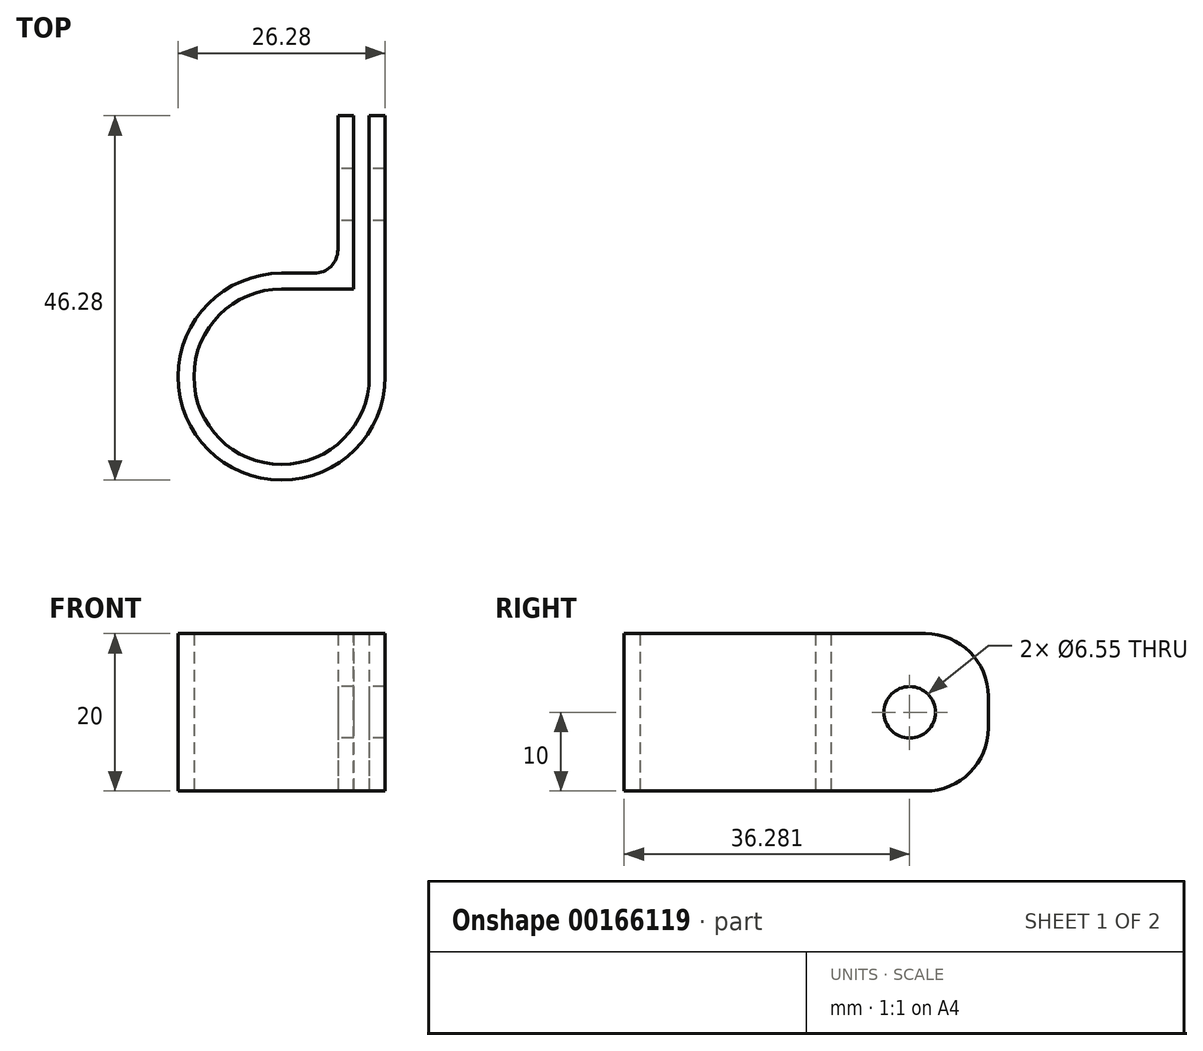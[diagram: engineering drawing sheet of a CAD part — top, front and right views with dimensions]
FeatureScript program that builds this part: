
annotation { "Feature Type Name" : "Feature", "Feature Type Description" : "" }
export const myFeature = defineFeature(function(context is Context, id is Id, definition is map)
    precondition{}
    {
        {
            var Q0;
            Q0=qCreatedBy(makeId("Top.planeOp"),FACE);
            var sketch = newSketch(context, id + "F0", { "sketchPlane" : qUnion([Q0])});
            skCircle(sketch, "E0", {"center": v(0, 0) * mm, "radius": 11.14 * mm});
            skCircle(sketch, "E1.0", {"center": v(0, 0) * mm, "radius": 13.14 * mm});
            skLineSegment(sketch, "E2", {"start": v(13.14, 0) * mm, "end": v(13.14, 33.14) * mm});
            skLineSegment(sketch, "E3", {"start": v(11.14, 0) * mm, "end": v(11.14, 33.14) * mm});
            skLineSegment(sketch, "E4", {"start": v(11.14, 33.14) * mm, "end": v(13.14, 33.14) * mm});
            skLineSegment(sketch, "E5", {"start": v(0, 13.14) * mm, "end": v(7.14, 13.14) * mm});
            skLineSegment(sketch, "E6", {"start": v(7.14, 13.14) * mm, "end": v(7.14, 33.14) * mm});
            skLineSegment(sketch, "E7", {"start": v(7.14, 33.14) * mm, "end": v(9.14, 33.14) * mm});
            skLineSegment(sketch, "E8", {"start": v(9.14, 33.14) * mm, "end": v(9.14, 9.44) * mm});
            skLineSegment(sketch, "E9", {"start": v(9.14, 33.14) * mm, "end": v(11.14, 33.14) * mm, "construction": true});
            skLineSegment(sketch, "E10", {"start": v(9.14, 9.44) * mm, "end": v(9.14, 6.37) * mm});
            skLineSegment(sketch, "E11", {"start": v(7.14, 23.14) * mm, "end": v(13.14, 23.14) * mm, "construction": true});
            skLineSegment(sketch, "E12", {"start": v(0, 11.14) * mm, "end": v(9.14, 11.14) * mm});
            skSolve(sketch);
        }
        {
            var Q0;
            {var subQ4=sQuery(id+"F0.wireOp",EDGE,"E0");var subQ7=sQuery(id+"F0.wireOp",EDGE,"E3");var subQ9=makeQuery(id+"F0.imprint","INTERSECT",VERTEX,{"derivedFrom":[subQ4,subQ7]});Q0=makeQuery(id+"F0.imprint","IMPRINT",FACE,{"disambiguationData":[TD([[makeQuery(id+"F0.imprint","IMPRINT",EDGE,{"disambiguationData":[TD([[subQ9,1.0]])],"derivedFrom":subQ4}),-1.0]])]});}
            var Q1;
            {var subQ1=sQuery(id+"F0.wireOp",EDGE,"E5");Q1=makeQuery(id+"F0.imprint","IMPRINT",FACE,{"disambiguationData":[TD([[makeQuery(id+"F0.imprint","IMPRINT",EDGE,{"derivedFrom":subQ1}),-1.0]])]});}
            var Q2;
            {var subQ0=sQuery(id+"F0.wireOp",EDGE,"E2");Q2=makeQuery(id+"F0.imprint","IMPRINT",FACE,{"disambiguationData":[TD([[makeQuery(id+"F0.imprint","IMPRINT",EDGE,{"derivedFrom":subQ0}),1.0]])]});}
            extrude(context, id + "F1", {"entities" : qUnion([Q0, Q1, Q2]), "endBound" : BoundingType.SYMMETRIC, "depth" : 20 * mm});
        }
        {
            var Q0;
            Q0=qCreatedBy(makeId("Right.planeOp"),FACE);
            var sketch = newSketch(context, id + "F2", { "sketchPlane" : qUnion([Q0])});
            skPoint(sketch, "E13.0", {"position": v(23.14, 0) * mm});
            skCircle(sketch, "E14", {"center": v(23.14, 0) * mm, "radius": 3.28 * mm});
            skSolve(sketch);
        }
        {
            var Q0;
            Q0 = qSketchRegion(id + "F2", true);
            extrude(context, id + "F3", {"entities" : qUnion([Q0]), "operationType" : NewBodyOperationType.REMOVE, "endBound" : BoundingType.THROUGH_ALL, "depth" : 25 * mm});
        }
        {
            var Q0;
            Q0=makeQuery(id+"F1.opExtrude","SWEPT_EDGE",EDGE,{"disambiguationData":[OSD([sQuery(id+"F0.wireOp",EDGE,"E5"),sQuery(id+"F0.wireOp",EDGE,"E6")])]});
            fillet(context, id + "F4", {"entities" : qUnion([Q0]), "radius" : 3 * mm, "allowEdgeOverflow" : false});
        }
        {
            var Q0;
            Q0=makeQuery(id+"F1.opExtrude","CAP_EDGE",EDGE,{"disambiguationData":[OSD([sQuery(id+"F0.wireOp",EDGE,"E7")])],"isStart":false});
            var Q1;
            Q1=makeQuery(id+"F1.opExtrude","CAP_EDGE",EDGE,{"disambiguationData":[OSD([sQuery(id+"F0.wireOp",EDGE,"E4")])],"isStart":false});
            var Q2;
            Q2=makeQuery(id+"F1.opExtrude","CAP_EDGE",EDGE,{"disambiguationData":[OSD([sQuery(id+"F0.wireOp",EDGE,"E4")])],"isStart":true});
            var Q3;
            Q3=makeQuery(id+"F1.opExtrude","CAP_EDGE",EDGE,{"disambiguationData":[OSD([sQuery(id+"F0.wireOp",EDGE,"E7")])],"isStart":true});
            fillet(context, id + "F5", {"entities" : qUnion([Q0, Q1, Q2, Q3]), "radius" : 8 * mm, "allowEdgeOverflow" : false});
        }
    });
